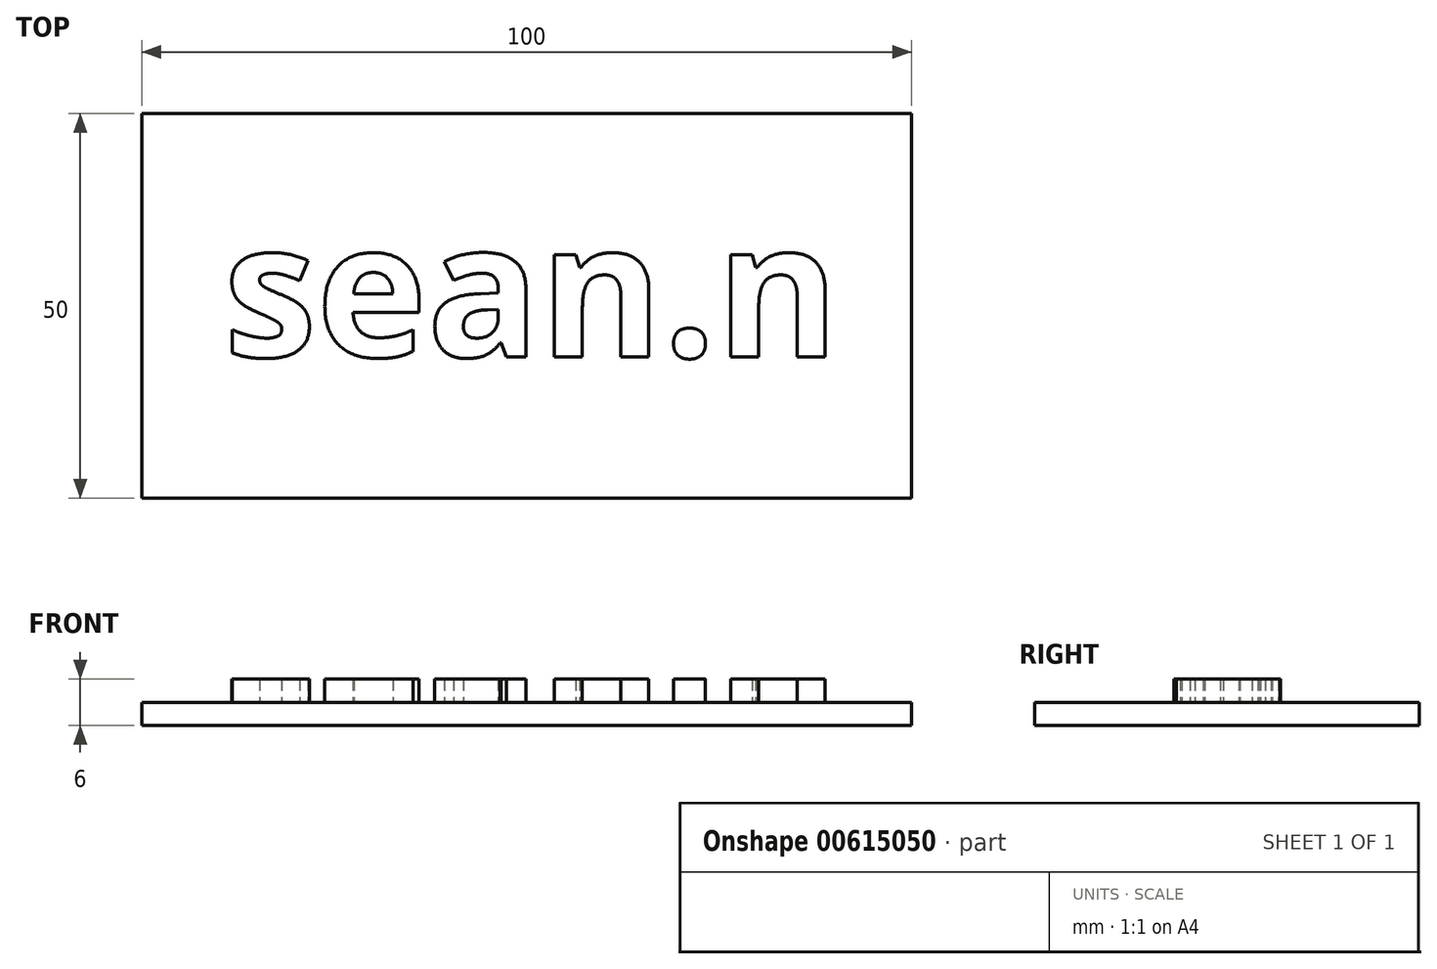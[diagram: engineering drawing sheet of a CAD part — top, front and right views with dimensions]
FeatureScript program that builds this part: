
annotation { "Feature Type Name" : "Feature", "Feature Type Description" : "" }
export const myFeature = defineFeature(function(context is Context, id is Id, definition is map)
    precondition{}
    {
        {
            var Q0;
            Q0=qCreatedBy(makeId("Top.planeOp"),FACE);
            var sketch = newSketch(context, id + "F0", { "sketchPlane" : qUnion([Q0])});
            skLineSegment(sketch, "E0.bottom", {"start": v(100, 50) * mm, "end": v(0, 50) * mm});
            skLineSegment(sketch, "E0.top", {"start": v(100, 0) * mm, "end": v(0, 0) * mm});
            skLineSegment(sketch, "E0.left", {"start": v(100, 50) * mm, "end": v(100, 0) * mm});
            skLineSegment(sketch, "E0.right", {"start": v(0, 50) * mm, "end": v(0, 0) * mm});
            skSolve(sketch);
        }
        {
            var Q0;
            Q0=makeQuery(id+"F0.imprint","IMPRINT",FACE,{"disambiguationData":[TD([[makeQuery(id+"F0.imprint","IMPRINT",EDGE,{"derivedFrom":sQuery(id+"F0.wireOp",EDGE,"E0.bottom")}),1.0]])]});
            extrude(context, id + "F1", {"entities" : qUnion([Q0]), "depth" : 3 * mm, "offsetDistance" : 25 * mm});
        }
        {
            var Q0;
            Q0=makeQuery(id+"F1.opExtrude","CAP_FACE",FACE,{"disambiguationData":[OSD([sQuery(id+"F0.wireOp",EDGE,"E0.bottom"),sQuery(id+"F0.wireOp",EDGE,"E0.top"),sQuery(id+"F0.wireOp",EDGE,"E0.left"),sQuery(id+"F0.wireOp",EDGE,"E0.right")])],"isStart":false});
            var sketch = newSketch(context, id + "F2", { "sketchPlane" : qUnion([Q0])});
            skText(sketch, "E1", { "text": "sean.n\n", "fontName": "OpenSans-Bold.ttf"});
            const initialGuessF2  = {"E1": [0.0106, 0.0184, 1, 0, 0.0175]};
            skSetInitialGuess(sketch, initialGuessF2);
            skSolve(sketch);
        }
        {
            var Q0;
            Q0 = qSketchRegion(id + "F2", true);
            extrude(context, id + "F3", {"entities" : qUnion([Q0]), "operationType" : NewBodyOperationType.ADD, "depth" : 3 * mm, "offsetDistance" : 25 * mm});
        }
    });
